# Revit family: KR6115551 Percha Koral niquel
name_source: partatom
category: Generic Models
units: mm (PartAtom-declared; Revit-internal decimal feet)

## family parameters
Always vertical = Yes
Can host rebar = No
Cut with Voids When Loaded = No
Host = Wall
Part Type = Normal
Room Calculation Point = No
Round Connector Dimension = Use Diameter
Shared = No

## types (1)
- Niquel
    Alto = 1500 mm  [stored 4.92126 ft]
    Colección = Accesorios 2016
    Creado por = IDD
    Description = La percha Koral te dará mayor seguridad y funcionalidad con una resistencia a la carga hasta de 9kg y sistema de fijación oculto. ¡Conócela ahora!
    Fecha de creación = 09/10/2020
    Garantía = 30 años en estructura
    Garantía Acabados = 3 años en acabado
    Línea = Koral
    Manufacturer = Corona
    Material = Corona_Niquel
    Peso Neto aprox = 180 g
    Referencia = KR6115551
    Resistencia = Resistente a la corrosión, pelado y decoloración por agua
    Resistencia a cargas = 9 Kg - 19,8 lb
    Temperaturas máxima de trabajo = 40˚C / 104˚F
    Temperaturas mínima de trabajo = 4˚C / 39,2˚F
    URL = https://corona.co

note: [stored X ft] marks values corroborated as IEEE doubles in the binary element streams (Revit-internal decimal feet)

## geometry (parser evidence)
native form markers: Sweep x2
no freeform markers — native parametric forms only
